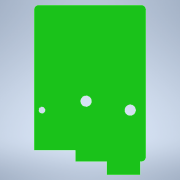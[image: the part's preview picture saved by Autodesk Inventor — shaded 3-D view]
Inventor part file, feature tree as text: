
AUTODESK INVENTOR PART (.ipt)
format: ipt  version: 2022 (Build 260153000, 153)  size: 156,160 bytes
history: native  units: mm
features: extrude x2, sketch x2, fillet x1
ambient origin geometry x8: Origin, YZ Plane, XZ Plane, XY Plane, X Axis, Y Axis, Z Axis, Center Point
bodies: Body1 (feature_tree)
feature tree (5):
  extrude  "Extrusion3"  Depth=70.0mm
  fillet  "Fillet1"  Radius=6.0mm
  extrude  "Extrusion10"  Depth=18.5mm
  sketch  "Sketch2"  dims[d0=50.0mm d1=70.0mm d12=6.0mm d13=0.0mm]
  sketch  "Sketch4"  dims[d14=2.0mm d16=18.5mm d17=5.0mm d31=5.0mm d34=3.0mm d41=5.0mm d44=19.75mm d45=19.75mm d46=7.0mm d58=2.5mm d59=15.0mm d60=6.0mm d61=23.0mm d62=27.0mm d63=23.0mm d64=0.0mm d65=0.0mm d4=0.0mm d5=0.0mm d6=0.0mm d7=0.0mm]
